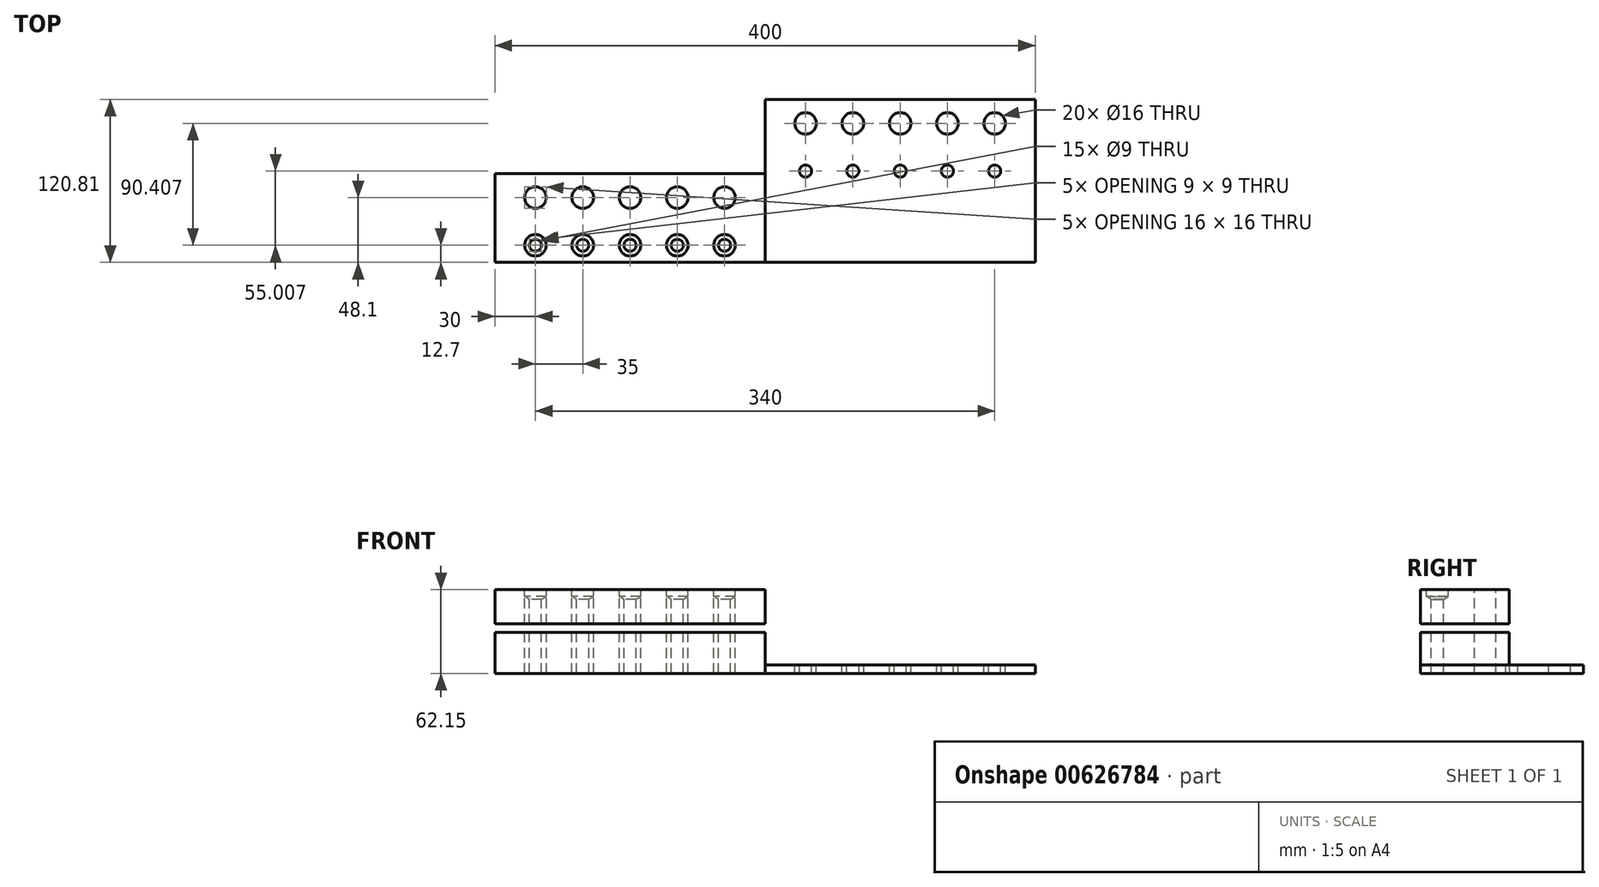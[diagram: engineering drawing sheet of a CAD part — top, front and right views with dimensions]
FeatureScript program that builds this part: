
annotation { "Feature Type Name" : "Feature", "Feature Type Description" : "" }
export const myFeature = defineFeature(function(context is Context, id is Id, definition is map)
    precondition{}
    {
        {
            var Q0;
            Q0=qCreatedBy(makeId("Top.planeOp"),FACE);
            var sketch = newSketch(context, id + "F0", { "sketchPlane" : qUnion([Q0])});
            skLineSegment(sketch, "E0.bottom", {"start": v(0, 0) * mm, "end": v(200, 0) * mm});
            skLineSegment(sketch, "E0.top", {"start": v(0, 120.81) * mm, "end": v(200, 120.81) * mm});
            skLineSegment(sketch, "E0.left", {"start": v(0, 0) * mm, "end": v(0, 120.81) * mm});
            skLineSegment(sketch, "E0.right", {"start": v(200, 0) * mm, "end": v(200, 120.81) * mm});
            skSolve(sketch);
        }
        {
            var Q0;
            Q0=makeQuery(id+"F0.imprint","IMPRINT",FACE,{"disambiguationData":[TD([[makeQuery(id+"F0.imprint","IMPRINT",EDGE,{"derivedFrom":sQuery(id+"F0.wireOp",EDGE,"E0.bottom")}),1.0]])]});
            extrude(context, id + "F1", {"entities" : qUnion([Q0]), "depth" : 6.35 * mm, "offsetDistance" : 25.4 * mm});
        }
        {
            var Q0;
            Q0=makeQuery(id+"F1.opExtrude","CAP_FACE",FACE,{"disambiguationData":[OSD([sQuery(id+"F0.wireOp",EDGE,"E0.bottom"),sQuery(id+"F0.wireOp",EDGE,"E0.top"),sQuery(id+"F0.wireOp",EDGE,"E0.left"),sQuery(id+"F0.wireOp",EDGE,"E0.right")])],"isStart":false});
            var sketch = newSketch(context, id + "F2", { "sketchPlane" : qUnion([Q0])});
            skCircle(sketch, "E1", {"center": v(30, 103.1) * mm, "radius": 5.32 * mm});
            skCircle(sketch, "E2", {"center": v(65, 103.1) * mm, "radius": 5.08 * mm});
            skCircle(sketch, "E3", {"center": v(100, 103.1) * mm, "radius": 5.62 * mm});
            skCircle(sketch, "E4", {"center": v(135, 103.1) * mm, "radius": 5.81 * mm});
            skCircle(sketch, "E5", {"center": v(170, 103.1) * mm, "radius": 6.05 * mm});
            skCircle(sketch, "E6", {"center": v(170, 67.7) * mm, "radius": 6.56 * mm});
            skCircle(sketch, "E7", {"center": v(135, 67.7) * mm, "radius": 7.65 * mm});
            skCircle(sketch, "E8", {"center": v(100, 67.7) * mm, "radius": 7.7 * mm});
            skCircle(sketch, "E9", {"center": v(65, 67.7) * mm, "radius": 7.25 * mm});
            skCircle(sketch, "E10", {"center": v(30, 67.7) * mm, "radius": 6.82 * mm});
            skSolve(sketch);
        }
        {
            var Q0;
            Q0=sQuery(id+"F2.wireOp",VERTEX,"E1.center");
            var Q1;
            Q1=sQuery(id+"F2.wireOp",VERTEX,"E2.center");
            var Q2;
            Q2=sQuery(id+"F2.wireOp",VERTEX,"E3.center");
            var Q3;
            Q3=sQuery(id+"F2.wireOp",VERTEX,"E4.center");
            var Q4;
            Q4=sQuery(id+"F2.wireOp",VERTEX,"E5.center");
            var Q5;
            Q5=makeQuery(id+"F1.opExtrude","SWEPT_BODY",BODY,{"disambiguationData":[OSD([sQuery(id+"F0.wireOp",EDGE,"E0.bottom"),sQuery(id+"F0.wireOp",EDGE,"E0.top"),sQuery(id+"F0.wireOp",EDGE,"E0.left"),sQuery(id+"F0.wireOp",EDGE,"E0.right")])]});
            hole(context, id + "F3", {"style" : HoleStyle.SIMPLE, "endStyle" : HoleEndStyle.THROUGH, "holeDiameter" : 16 * mm, "majorDiameter" : 6.35 * mm, "isTappedThrough" : true, "tappedDepth" : 12.7 * mm, "tapClearance" : 3, "locations" : qUnion([Q0, Q1, Q2, Q3, Q4]), "scope" : qUnion([Q5])});
        }
        {
            var Q0;
            Q0=qCreatedBy(makeId("Top.planeOp"),FACE);
            var sketch = newSketch(context, id + "F4", { "sketchPlane" : qUnion([Q0])});
            skLineSegment(sketch, "E11.bottom", {"start": v(0, 0) * mm, "end": v(-200, 0) * mm});
            skLineSegment(sketch, "E11.top", {"start": v(0, 65.8) * mm, "end": v(-200, 65.8) * mm});
            skLineSegment(sketch, "E11.left", {"start": v(0, 0) * mm, "end": v(0, 65.8) * mm});
            skLineSegment(sketch, "E11.right", {"start": v(-200, 0) * mm, "end": v(-200, 65.8) * mm});
            skSolve(sketch);
        }
        {
            var Q0;
            Q0=makeQuery(id+"F4.imprint","IMPRINT",FACE,{"disambiguationData":[TD([[makeQuery(id+"F4.imprint","IMPRINT",EDGE,{"derivedFrom":sQuery(id+"F4.wireOp",EDGE,"E11.bottom")}),-1.0]])]});
            extrude(context, id + "F5", {"entities" : qUnion([Q0]), "depth" : 62.15 * mm, "offsetDistance" : 25.4 * mm});
        }
        {
            var Q0;
            Q0=makeQuery(id+"F5.opExtrude","CAP_FACE",FACE,{"disambiguationData":[OSD([sQuery(id+"F4.wireOp",EDGE,"E11.bottom"),sQuery(id+"F4.wireOp",EDGE,"E11.top"),sQuery(id+"F4.wireOp",EDGE,"E11.left"),sQuery(id+"F4.wireOp",EDGE,"E11.right")])],"isStart":false});
            var sketch = newSketch(context, id + "F6", { "sketchPlane" : qUnion([Q0])});
            skLineSegment(sketch, "E12", {"start": v(-200, 25.4) * mm, "end": v(0, 25.4) * mm});
            skCircle(sketch, "E13", {"center": v(-170, 12.7) * mm, "radius": 7.39 * mm});
            skCircle(sketch, "E14", {"center": v(-135, 12.7) * mm, "radius": 7.19 * mm});
            skCircle(sketch, "E15", {"center": v(-100, 12.7) * mm, "radius": 7.36 * mm});
            skCircle(sketch, "E16", {"center": v(-65, 12.7) * mm, "radius": 7.39 * mm});
            skCircle(sketch, "E17", {"center": v(-30, 12.7) * mm, "radius": 7.5 * mm});
            skCircle(sketch, "E18", {"center": v(-170, 48.1) * mm, "radius": 6.88 * mm});
            skCircle(sketch, "E19", {"center": v(-135, 48.1) * mm, "radius": 6.39 * mm});
            skCircle(sketch, "E20", {"center": v(-100, 48.1) * mm, "radius": 6.22 * mm});
            skCircle(sketch, "E21", {"center": v(-65, 48.1) * mm, "radius": 7.21 * mm});
            skCircle(sketch, "E22", {"center": v(-30, 48.1) * mm, "radius": 7.16 * mm});
            skSolve(sketch);
        }
        {
            var Q0;
            Q0=sQuery(id+"F6.wireOp",VERTEX,"E13.center");
            var Q1;
            Q1=sQuery(id+"F6.wireOp",VERTEX,"E14.center");
            var Q2;
            Q2=sQuery(id+"F6.wireOp",VERTEX,"E15.center");
            var Q3;
            Q3=sQuery(id+"F6.wireOp",VERTEX,"E16.center");
            var Q4;
            Q4=sQuery(id+"F6.wireOp",VERTEX,"E17.center");
            var Q5;
            Q5=makeQuery(id+"F5.opExtrude","SWEPT_BODY",BODY,{"disambiguationData":[OSD([sQuery(id+"F4.wireOp",EDGE,"E11.bottom"),sQuery(id+"F4.wireOp",EDGE,"E11.top"),sQuery(id+"F4.wireOp",EDGE,"E11.left"),sQuery(id+"F4.wireOp",EDGE,"E11.right")])]});
            hole(context, id + "F7", {"style" : HoleStyle.SIMPLE, "endStyle" : HoleEndStyle.THROUGH, "holeDiameter" : 9 * mm, "majorDiameter" : 6.35 * mm, "isTappedThrough" : true, "tappedDepth" : 12.7 * mm, "tapClearance" : 3, "locations" : qUnion([Q0, Q1, Q2, Q3, Q4]), "scope" : qUnion([Q5])});
        }
        {
            var Q0;
            Q0=sQuery(id+"F6.wireOp",VERTEX,"E18.center");
            var Q1;
            Q1=sQuery(id+"F6.wireOp",VERTEX,"E19.center");
            var Q2;
            Q2=sQuery(id+"F6.wireOp",VERTEX,"E20.center");
            var Q3;
            Q3=sQuery(id+"F6.wireOp",VERTEX,"E21.center");
            var Q4;
            Q4=sQuery(id+"F6.wireOp",VERTEX,"E22.center");
            var Q5;
            Q5=makeQuery(id+"F5.opExtrude","SWEPT_BODY",BODY,{"disambiguationData":[OSD([sQuery(id+"F4.wireOp",EDGE,"E11.bottom"),sQuery(id+"F4.wireOp",EDGE,"E11.top"),sQuery(id+"F4.wireOp",EDGE,"E11.left"),sQuery(id+"F4.wireOp",EDGE,"E11.right")])]});
            hole(context, id + "F8", {"style" : HoleStyle.SIMPLE, "endStyle" : HoleEndStyle.THROUGH, "holeDiameter" : 16 * mm, "majorDiameter" : 6.35 * mm, "isTappedThrough" : true, "tappedDepth" : 12.7 * mm, "tapClearance" : 3, "locations" : qUnion([Q0, Q1, Q2, Q3, Q4]), "scope" : qUnion([Q5])});
        }
        {
            var Q0;
            Q0=makeQuery(id+"F5.opExtrude","SWEPT_FACE",FACE,{"disambiguationData":[OSD([sQuery(id+"F4.wireOp",EDGE,"E11.left")])]});
            var sketch = newSketch(context, id + "F9", { "sketchPlane" : qUnion([Q0])});
            skLineSegment(sketch, "E23.bottom", {"start": v(0, 30.4) * mm, "end": v(25.4, 30.4) * mm});
            skLineSegment(sketch, "E23.top", {"start": v(0, 36.75) * mm, "end": v(25.4, 36.75) * mm});
            skLineSegment(sketch, "E23.left", {"start": v(0, 30.4) * mm, "end": v(0, 36.75) * mm});
            skLineSegment(sketch, "E23.right", {"start": v(25.4, 30.4) * mm, "end": v(25.4, 36.75) * mm});
            skSolve(sketch);
        }
        {
            var Q0;
            Q0=makeQuery(id+"F9.imprint","IMPRINT",FACE,{"disambiguationData":[TD([[makeQuery(id+"F9.imprint","IMPRINT",EDGE,{"derivedFrom":sQuery(id+"F9.wireOp",EDGE,"E23.bottom")}),1.0]])]});
            extrude(context, id + "F10", {"entities" : qUnion([Q0]), "operationType" : NewBodyOperationType.REMOVE, "oppositeDirection" : true, "depth" : 200 * mm, "offsetDistance" : 25.4 * mm});
        }
        {
            var Q0;
            Q0=sQuery(id+"F6.wireOp",VERTEX,"E13.center");
            var Q1;
            Q1=sQuery(id+"F6.wireOp",VERTEX,"E14.center");
            var Q2;
            Q2=sQuery(id+"F6.wireOp",VERTEX,"E15.center");
            var Q3;
            Q3=sQuery(id+"F6.wireOp",VERTEX,"E16.center");
            var Q4;
            Q4=sQuery(id+"F6.wireOp",VERTEX,"E17.center");
            var Q5;
            Q5=makeQuery(id+"F5.opExtrude","SWEPT_BODY",BODY,{"disambiguationData":[OSD([sQuery(id+"F4.wireOp",EDGE,"E11.bottom"),sQuery(id+"F4.wireOp",EDGE,"E11.top"),sQuery(id+"F4.wireOp",EDGE,"E11.left"),sQuery(id+"F4.wireOp",EDGE,"E11.right")])]});
            hole(context, id + "F11", {"style" : HoleStyle.SIMPLE, "endStyle" : HoleEndStyle.BLIND, "holeDiameter" : 16 * mm, "majorDiameter" : 6.35 * mm, "holeDepth" : 5 * mm, "isTappedThrough" : true, "tappedDepth" : 12.7 * mm, "tapClearance" : 3, "locations" : qUnion([Q0, Q1, Q2, Q3, Q4]), "scope" : qUnion([Q5])});
        }
        {
            var Q0;
            Q0=makeQuery(id+"F5.opExtrude","SWEPT_FACE",FACE,{"disambiguationData":[OSD([sQuery(id+"F4.wireOp",EDGE,"E11.left")])]});
            var sketch = newSketch(context, id + "F12", { "sketchPlane" : qUnion([Q0])});
            skLineSegment(sketch, "E24.bottom", {"start": v(25.4, 30.4) * mm, "end": v(65.8, 30.4) * mm});
            skLineSegment(sketch, "E24.top", {"start": v(25.4, 36.75) * mm, "end": v(65.8, 36.75) * mm});
            skLineSegment(sketch, "E24.left", {"start": v(25.4, 30.4) * mm, "end": v(25.4, 36.75) * mm});
            skLineSegment(sketch, "E24.right", {"start": v(65.8, 30.4) * mm, "end": v(65.8, 36.75) * mm});
            skSolve(sketch);
        }
        {
            var Q0;
            Q0=makeQuery(id+"F12.imprint","IMPRINT",FACE,{"disambiguationData":[TD([[makeQuery(id+"F12.imprint","IMPRINT",EDGE,{"derivedFrom":sQuery(id+"F12.wireOp",EDGE,"E24.bottom")}),1.0]])]});
            extrude(context, id + "F13", {"entities" : qUnion([Q0]), "operationType" : NewBodyOperationType.REMOVE, "endBound" : BoundingType.THROUGH_ALL, "oppositeDirection" : true, "depth" : 25.4 * mm, "offsetDistance" : 25.4 * mm});
        }
        {
            var Q0;
            Q0=sQuery(id+"F2.wireOp",VERTEX,"E8.center");
            var Q1;
            Q1=sQuery(id+"F2.wireOp",VERTEX,"E7.center");
            var Q2;
            Q2=sQuery(id+"F2.wireOp",VERTEX,"E6.center");
            var Q3;
            Q3=sQuery(id+"F2.wireOp",VERTEX,"E9.center");
            var Q4;
            Q4=sQuery(id+"F2.wireOp",VERTEX,"E10.center");
            var Q5;
            Q5=makeQuery(id+"F1.opExtrude","SWEPT_BODY",BODY,{"disambiguationData":[OSD([sQuery(id+"F0.wireOp",EDGE,"E0.bottom"),sQuery(id+"F0.wireOp",EDGE,"E0.top"),sQuery(id+"F0.wireOp",EDGE,"E0.left"),sQuery(id+"F0.wireOp",EDGE,"E0.right")])]});
            hole(context, id + "F14", {"style" : HoleStyle.SIMPLE, "endStyle" : HoleEndStyle.THROUGH, "holeDiameter" : 9 * mm, "majorDiameter" : 6.35 * mm, "isTappedThrough" : true, "tappedDepth" : 12.7 * mm, "tapClearance" : 3, "locations" : qUnion([Q0, Q1, Q2, Q3, Q4]), "scope" : qUnion([Q5])});
        }
    });
